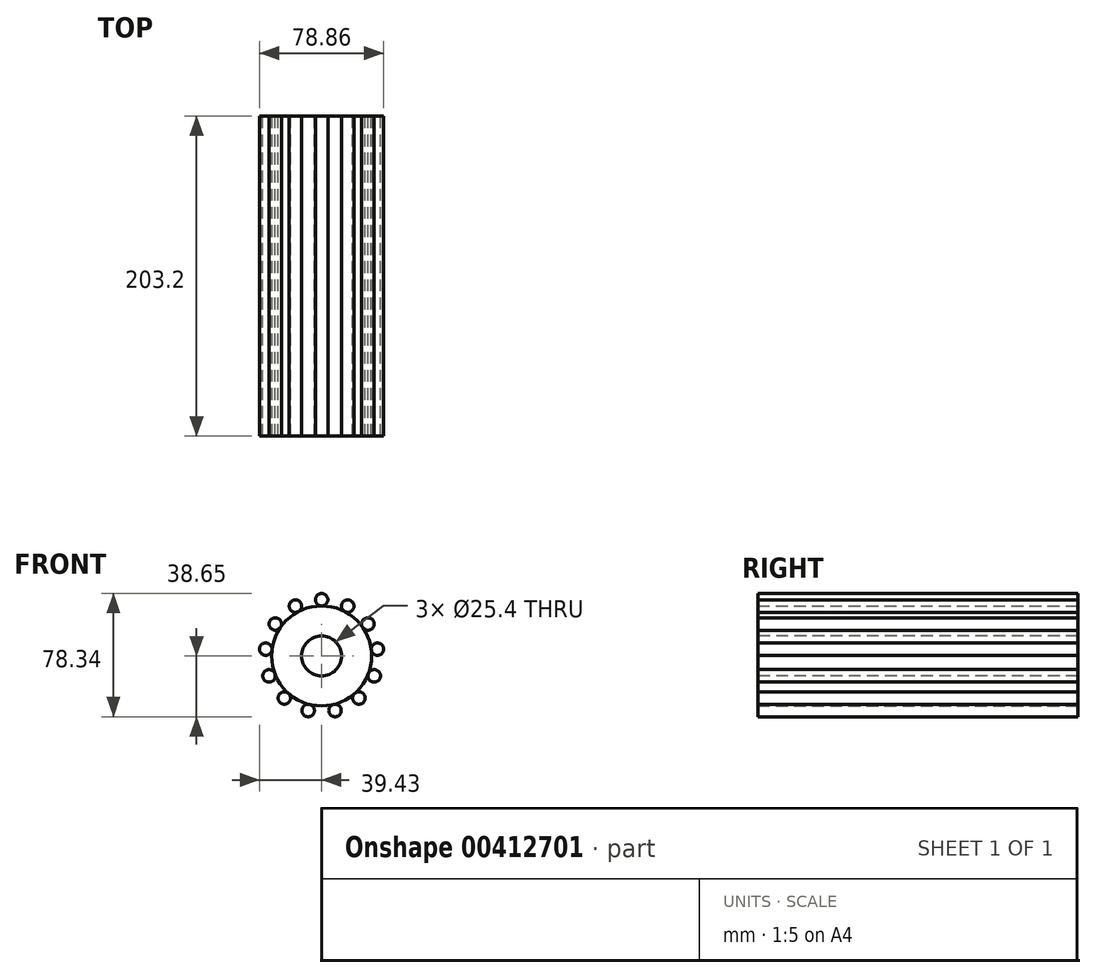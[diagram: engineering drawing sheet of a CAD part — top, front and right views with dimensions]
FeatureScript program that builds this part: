
annotation { "Feature Type Name" : "Feature", "Feature Type Description" : "" }
export const myFeature = defineFeature(function(context is Context, id is Id, definition is map)
    precondition{}
    {
        {
            var Q0;
            Q0=qCreatedBy(makeId("Front.planeOp"),FACE);
            var sketch = newSketch(context, id + "F0", { "sketchPlane" : qUnion([Q0])});
            skCircle(sketch, "E0", {"center": v(0, 0) * mm, "radius": 31.75 * mm});
            skPoint(sketch, "E1.center.orphan", {"position": v(0, 31.75) * mm});
            skCircle(sketch, "E2", {"center": v(0, 35.72) * mm, "radius": 3.97 * mm});
            skCircle(sketch, "E3.1.0", {"center": v(-16.6, 31.63) * mm, "radius": 3.97 * mm});
            skCircle(sketch, "E3.2.0", {"center": v(-29.4, 20.3) * mm, "radius": 3.97 * mm});
            skCircle(sketch, "E3.3.0", {"center": v(-35.46, 4.3) * mm, "radius": 3.97 * mm});
            skCircle(sketch, "E3.4.0", {"center": v(-33.4, -12.67) * mm, "radius": 3.97 * mm});
            skCircle(sketch, "E3.5.0", {"center": v(-23.69, -26.74) * mm, "radius": 3.97 * mm});
            skCircle(sketch, "E3.6.0", {"center": v(-8.55, -34.68) * mm, "radius": 3.97 * mm});
            skCircle(sketch, "E3.7.0", {"center": v(8.55, -34.68) * mm, "radius": 3.97 * mm});
            skCircle(sketch, "E3.8.0", {"center": v(23.69, -26.74) * mm, "radius": 3.97 * mm});
            skCircle(sketch, "E3.9.0", {"center": v(33.4, -12.67) * mm, "radius": 3.97 * mm});
            skCircle(sketch, "E3.10.0", {"center": v(35.46, 4.3) * mm, "radius": 3.97 * mm});
            skCircle(sketch, "E3.11.0", {"center": v(29.4, 20.3) * mm, "radius": 3.97 * mm});
            skCircle(sketch, "E3.12.0", {"center": v(16.6, 31.63) * mm, "radius": 3.97 * mm});
            skSolve(sketch);
        }
        {
            var Q0;
            Q0 = qSketchRegion(id + "F0", true);
            extrude(context, id + "F1", {"entities" : qUnion([Q0]), "depth" : 203.2 * mm});
        }
        {
            var Q0;
            Q0=makeQuery(id+"F1.opExtrude","CAP_FACE",FACE,{"disambiguationData":[OSD([sQuery(id+"F0.wireOp",EDGE,"E0")])],"isStart":false});
            var sketch = newSketch(context, id + "F2", { "sketchPlane" : qUnion([Q0])});
            skCircle(sketch, "E4", {"center": v(0, 0) * mm, "radius": 12.7 * mm});
            skSolve(sketch);
        }
        {
            var Q0;
            Q0 = qSketchRegion(id + "F2", true);
            extrude(context, id + "F3", {"entities" : qUnion([Q0]), "operationType" : NewBodyOperationType.REMOVE, "oppositeDirection" : true, "depth" : 203.2 * mm});
        }
    });
